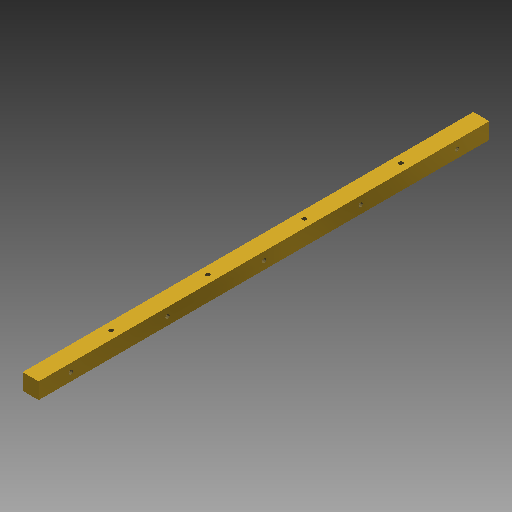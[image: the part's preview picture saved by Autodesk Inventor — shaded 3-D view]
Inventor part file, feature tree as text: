
AUTODESK INVENTOR PART (.ipt)
format: ipt  version: 2017 (Build 210142000, 142)  size: 110,080 bytes
history: native  units: in
note: dims shown in document units (in); Inventor stores cm internally (conversion verified against a paired STEP export)
features: sketch x3, hole x2, pattern_linear x2, extrude x1
ambient origin geometry x8: Origin, YZ Plane, XZ Plane, XY Plane, X Axis, Y Axis, Z Axis, Center Point
bodies: Solid1 (feature_tree)
feature tree (8):
  extrude  "Extrusion1"  Depth=0.25in
  hole  "Hole1"  [1 undecoded]
  pattern_linear  "Rectangular Pattern1"  Count1=5 Spacing1=1.5in
  pattern_linear  "Rectangular Pattern2"  Spacing1=0.75in  [1 undecoded]
  sketch  "Sketch1"  dims[d0=0.25in d2=0.25in]
  sketch  "Sketch2"  dims[d3=7.0in d4=0.0in d5=0.125in]
  sketch  "Sketch3"  dims[d6=0.5in d7=0.067in d8=0.75in d9=0.375in d10=0.25in d11=0.5635in d12=1.0in d13=0.8108in d21=1.9685in d23=1.5in d24=0.75in d27=0.8108in d28=0.5635in d29=0.25in d30=0.375in d31=1.0in d32=0.067in d33=1.25in d34=1.5748in d36=1.5in d37=0.125in]
  hole  "Hole2"  [1 undecoded]
note: 3 required parameter values undecoded (feature->parameter linkage not recoverable at this tier; creation-order binding heuristic only, values carry confidence <= 0.55)
